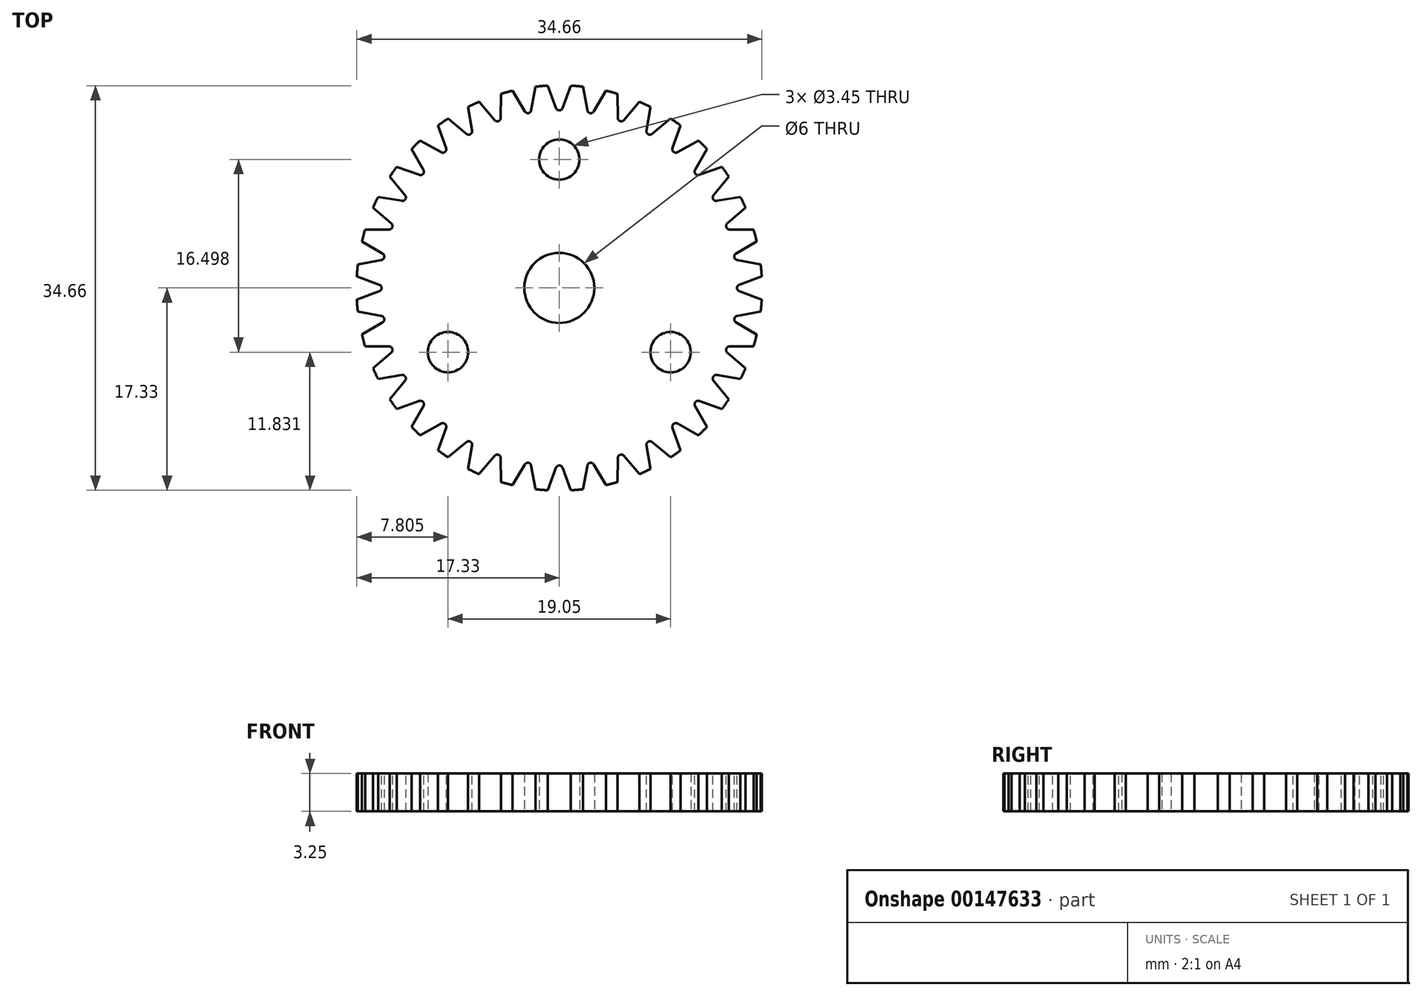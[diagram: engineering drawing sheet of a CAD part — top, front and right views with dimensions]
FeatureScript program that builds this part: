
annotation { "Feature Type Name" : "Feature", "Feature Type Description" : "" }
export const myFeature = defineFeature(function(context is Context, id is Id, definition is map)
    precondition{}
    {
        {
            var Q0;
            Q0=qCreatedBy(makeId("Top.planeOp"),FACE);
            var sketch = newSketch(context, id + "F0", { "sketchPlane" : qUnion([Q0])});
            skCircle(sketch, "E0", {"center": v(0, 0) * mm, "radius": 17.36 * mm});
            skCircle(sketch, "E1.cCircle", {"center": v(0, 0) * mm, "radius": 5.5 * mm, "construction": true});
            skLineSegment(sketch, "E1.0", {"start": v(9.52, -5.5) * mm, "end": v(-9.52, -5.5) * mm, "construction": true});
            skLineSegment(sketch, "E1.1", {"start": v(-9.52, -5.5) * mm, "end": v(0, 11) * mm, "construction": true});
            skLineSegment(sketch, "E1.2", {"start": v(0, 11) * mm, "end": v(9.52, -5.5) * mm, "construction": true});
            skPoint(sketch, "E1.0.midPoint", {"position": v(0, -5.5) * mm});
            skCircle(sketch, "E2", {"center": v(0, 0) * mm, "radius": 14.97 * mm, "construction": true});
            skCircle(sketch, "E3", {"center": v(0, 11) * mm, "radius": 3.97 * mm, "construction": true});
            skCircle(sketch, "E4", {"center": v(0, 11) * mm, "radius": 1.73 * mm});
            skCircle(sketch, "E5", {"center": v(9.52, -5.5) * mm, "radius": 1.73 * mm});
            skCircle(sketch, "E6", {"center": v(-9.52, -5.5) * mm, "radius": 1.73 * mm});
            skCircle(sketch, "E7", {"center": v(0, 0) * mm, "radius": 3 * mm});
            skSolve(sketch);
        }
        {
            var Q0;
            Q0=qSketchRegion(id+"F0",true);
            extrude(context, id + "F1", {"entities" : qUnion([Q0]), "depth" : 3.25 * mm});
        }
        {
            var Q0;
            Q0=makeQuery(id+"F1.opExtrude","CAP_FACE",FACE,{"disambiguationData":[OSD([sQuery(id+"F0.wireOp",EDGE,"E0")])],"isStart":false});
            var sketch = newSketch(context, id + "F2", { "sketchPlane" : qUnion([Q0])});
            skLineSegment(sketch, "E8", {"start": v(0, 0) * mm, "end": v(0, 17.36) * mm});
            skArc(sketch, "E9", {"start": v(1, 17.33) * mm, "mid": v(0, 17.36) * mm, "end": v(-1, 17.33) * mm});
            skLineSegment(sketch, "E10", {"start": v(-1, 17.33) * mm, "end": v(-0.28, 15.4) * mm});
            skLineSegment(sketch, "E11", {"start": v(1, 17.33) * mm, "end": v(0.28, 15.4) * mm});
            skArc(sketch, "E12", {"start": v(-0.28, 15.4) * mm, "mid": v(0, 15.2) * mm, "end": v(0.28, 15.4) * mm});
            skLineSegment(sketch, "E13", {"start": v(0, 0) * mm, "end": v(0.68, 17.34) * mm, "construction": true});
            skPoint(sketch, "E14", {"position": v(0.64, 16.36) * mm});
            skSolve(sketch);
        }
        {
            var Q0;
            Q0=qSketchRegion(id+"F2",true);
            var Q1;
            Q1=makeQuery(id+"F1.opExtrude","CAP_FACE",FACE,{"disambiguationData":[OSD([sQuery(id+"F0.wireOp",EDGE,"E0")])],"isStart":true});
            extrude(context, id + "F3", {"entities" : qUnion([Q0]), "operationType" : NewBodyOperationType.REMOVE, "endBound" : BoundingType.UP_TO_SURFACE, "oppositeDirection" : true, "endBoundEntityFace" : qUnion([Q1]), "depth" : 25.4 * mm});
        }
        {
            var Q0;
            Q0=makeQuery(id+"F3.boolean.opBoolean","COPY",FACE,{"derivedFrom":makeQuery(id+"F3.opExtrude","SWEPT_FACE",FACE,{"disambiguationData":[OSD([sQuery(id+"F2.wireOp",EDGE,"E11")])]})});
            var Q1;
            Q1=makeQuery(id+"F3.boolean.opBoolean","COPY",FACE,{"derivedFrom":makeQuery(id+"F3.opExtrude","SWEPT_FACE",FACE,{"disambiguationData":[OSD([sQuery(id+"F2.wireOp",EDGE,"E12")])]})});
            var Q2;
            Q2=makeQuery(id+"F3.boolean.opBoolean","COPY",FACE,{"derivedFrom":makeQuery(id+"F3.opExtrude","SWEPT_FACE",FACE,{"disambiguationData":[OSD([sQuery(id+"F2.wireOp",EDGE,"E10")])]})});
            var Q3;
            Q3=makeQuery(id+"F1.opExtrude","SWEPT_FACE",FACE,{"disambiguationData":[OSD([sQuery(id+"F0.wireOp",EDGE,"E0")])]});
            circularPattern(context, id + "F4", {"patternType" : PatternType.FACE, "faces" : qUnion([Q0, Q1, Q2]), "axis" : qUnion([Q3]), "angle" : 10 * degree, "instanceCount" : 36});
        }
    });
